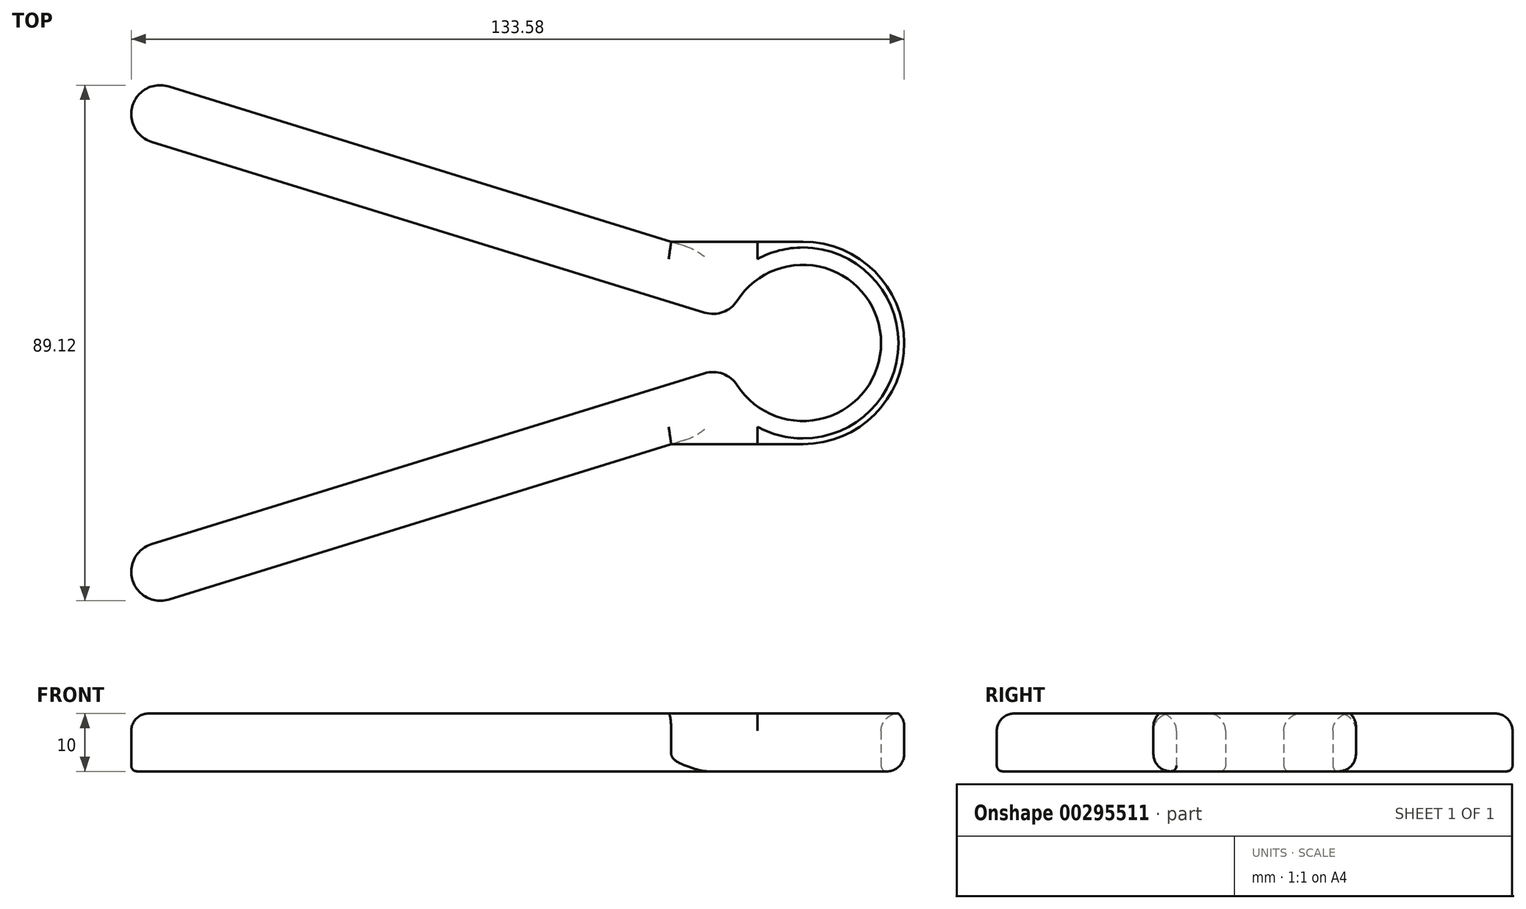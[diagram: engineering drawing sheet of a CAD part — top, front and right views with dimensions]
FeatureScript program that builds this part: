
annotation { "Feature Type Name" : "Feature", "Feature Type Description" : "" }
export const myFeature = defineFeature(function(context is Context, id is Id, definition is map)
    precondition{}
    {
        {
            var Q0;
            Q0=qCreatedBy(makeId("Top.planeOp"),FACE);
            var sketch = newSketch(context, id + "F0", { "sketchPlane" : qUnion([Q0])});
            skArc(sketch, "E0", {"start": v(-11.34, -7.32) * mm, "mid": v(13.5, 0) * mm, "end": v(-11.34, 7.32) * mm});
            skArc(sketch, "E1", {"start": v(-9.02, -15) * mm, "mid": v(17.5, 0) * mm, "end": v(-9.02, 15) * mm});
            skLineSegment(sketch, "E2", {"start": v(-17.02, 5.26) * mm, "end": v(-112.56, 34.78) * mm});
            skLineSegment(sketch, "E3.0", {"start": v(-13.07, 14.5) * mm, "end": v(-109.6, 44.33) * mm});
            skLineSegment(sketch, "E4.MirrorCS", {"start": v(-17.02, -5.26) * mm, "end": v(-112.56, -34.78) * mm});
            skLineSegment(sketch, "E5.MirrorCS", {"start": v(-13.07, -14.5) * mm, "end": v(-109.6, -44.33) * mm});
            skLineSegment(sketch, "E6", {"start": v(-115.86, 41.03) * mm, "end": v(-115.86, 41.03) * mm});
            skLineSegment(sketch, "E7", {"start": v(-115.86, -41.03) * mm, "end": v(-115.86, -41.03) * mm});
            skPoint(sketch, "E8.orphan", {"position": v(1.27, 10.08) * mm});
            skPoint(sketch, "E9.orphan", {"position": v(1.27, -10.08) * mm});
            skPoint(sketch, "E10.visualSharp", {"position": v(-114.39, 45.81) * mm});
            skArc(sketch, "E10.filletArc", {"start": v(-109.6, 44.33) * mm, "mid": v(-113.42, 43.98) * mm, "end": v(-115.86, 41.03) * mm});
            skPoint(sketch, "E11.visualSharp", {"position": v(-117.34, 36.26) * mm});
            skArc(sketch, "E11.filletArc", {"start": v(-115.86, 41.03) * mm, "mid": v(-115.5, 37.22) * mm, "end": v(-112.56, 34.78) * mm});
            skPoint(sketch, "E12.visualSharp", {"position": v(-117.34, -36.26) * mm});
            skArc(sketch, "E12.filletArc", {"start": v(-112.56, -34.78) * mm, "mid": v(-115.5, -37.22) * mm, "end": v(-115.86, -41.03) * mm});
            skPoint(sketch, "E13.visualSharp", {"position": v(-114.39, -45.81) * mm});
            skArc(sketch, "E13.filletArc", {"start": v(-115.86, -41.03) * mm, "mid": v(-113.42, -43.98) * mm, "end": v(-109.6, -44.33) * mm});
            skPoint(sketch, "E14.visualSharp", {"position": v(-10.77, 13.8) * mm});
            skArc(sketch, "E14.filletArc", {"start": v(-13.07, 14.5) * mm, "mid": v(-11, 14.32) * mm, "end": v(-9.02, 15) * mm});
            skPoint(sketch, "E15.visualSharp", {"position": v(-12.9, 3.99) * mm});
            skArc(sketch, "E15.filletArc", {"start": v(-17.02, 5.26) * mm, "mid": v(-13.83, 5.34) * mm, "end": v(-11.34, 7.32) * mm});
            skPoint(sketch, "E16.visualSharp", {"position": v(-12.9, -3.99) * mm});
            skArc(sketch, "E16.filletArc", {"start": v(-11.34, -7.32) * mm, "mid": v(-13.83, -5.34) * mm, "end": v(-17.02, -5.26) * mm});
            skPoint(sketch, "E17.visualSharp", {"position": v(-10.77, -13.8) * mm});
            skArc(sketch, "E17.filletArc", {"start": v(-9.02, -15) * mm, "mid": v(-11, -14.32) * mm, "end": v(-13.07, -14.5) * mm});
            skLineSegment(sketch, "E18", {"start": v(0, 17.5) * mm, "end": v(-22.76, 17.5) * mm});
            skLineSegment(sketch, "E19", {"start": v(0, -17.5) * mm, "end": v(-22.76, -17.5) * mm});
            skSolve(sketch);
        }
        {
            var Q0;
            Q0 = qSketchRegion(id + "F0", true);
            extrude(context, id + "F1", {"entities" : qUnion([Q0]), "depth" : 10 * mm});
        }
        {
            var Q0;
            Q0=makeQuery(id+"F1.opExtrude","CAP_EDGE",EDGE,{"disambiguationData":[OSD([sQuery(id+"F0.wireOp",EDGE,"E3.0")])],"isStart":false});
            var Q1;
            Q1=makeQuery(id+"F1.opExtrude","CAP_EDGE",EDGE,{"disambiguationData":[OSD([sQuery(id+"F0.wireOp",EDGE,"E5.MirrorCS")])],"isStart":false});
            fillet(context, id + "F2", {"entities" : qUnion([Q0, Q1]), "radius" : 3 * mm, "tangentPropagation" : true, "allowEdgeOverflow" : false});
        }
        {
            var Q0;
            Q0=makeQuery(id+"F1.opExtrude","CAP_EDGE",EDGE,{"disambiguationData":[OSD([sQuery(id+"F0.wireOp",EDGE,"E5.MirrorCS")])],"isStart":true});
            var Q1;
            Q1=makeQuery(id+"F1.opExtrude","CAP_EDGE",EDGE,{"disambiguationData":[OSD([sQuery(id+"F0.wireOp",EDGE,"E3.0")])],"isStart":true});
            fillet(context, id + "F3", {"entities" : qUnion([Q0, Q1]), "radius" : 1 * mm, "tangentPropagation" : true, "allowEdgeOverflow" : false});
        }
        {
            var Q0;
            Q0=makeQuery(id+"F1.opExtrude","CAP_EDGE",EDGE,{"disambiguationData":[OSD([sQuery(id+"F0.wireOp",EDGE,"E19")])],"isStart":false});
            var Q1;
            Q1=makeQuery(id+"F1.opExtrude","CAP_EDGE",EDGE,{"disambiguationData":[OSD([sQuery(id+"F0.wireOp",EDGE,"E19")])],"isStart":true});
            fillet(context, id + "F4", {"entities" : qUnion([Q0, Q1]), "radius" : 3 * mm, "tangentPropagation" : true, "allowEdgeOverflow" : false});
        }
    });
